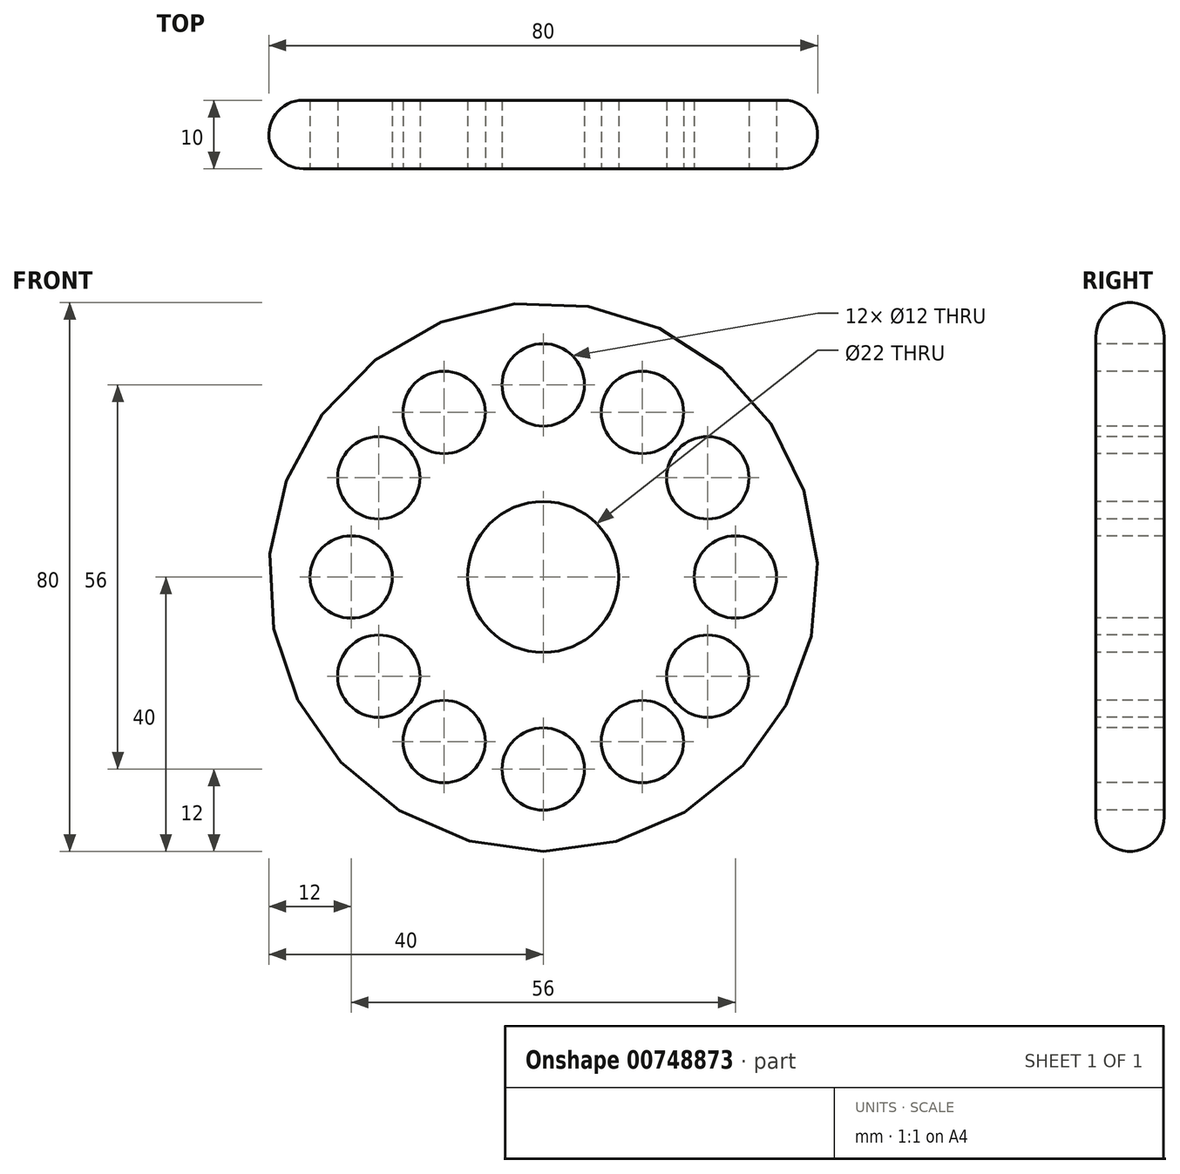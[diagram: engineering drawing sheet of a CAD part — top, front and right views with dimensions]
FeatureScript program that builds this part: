
annotation { "Feature Type Name" : "Feature", "Feature Type Description" : "" }
export const myFeature = defineFeature(function(context is Context, id is Id, definition is map)
    precondition{}
    {
        {
            var Q0;
            Q0=qCreatedBy(makeId("Front.planeOp"),FACE);
            var sketch = newSketch(context, id + "F0", { "sketchPlane" : qUnion([Q0])});
            skCircle(sketch, "E0", {"center": v(0, 0) * mm, "radius": 40 * mm});
            skSolve(sketch);
        }
        {
            var Q0;
            Q0=makeQuery(id+"F0.imprint","IMPRINT",FACE,{"disambiguationData":[TD([[makeQuery(id+"F0.imprint","IMPRINT",EDGE,{"derivedFrom":sQuery(id+"F0.wireOp",EDGE,"E0")}),1.0]])]});
            extrude(context, id + "F1", {"entities" : qUnion([Q0]), "endBound" : BoundingType.SYMMETRIC, "depth" : 10 * mm, "offsetDistance" : 25 * mm});
        }
        {
            var Q0;
            Q0=makeQuery(id+"F1.opExtrude","CAP_FACE",FACE,{"disambiguationData":[OSD([sQuery(id+"F0.wireOp",EDGE,"E0")])],"isStart":false});
            var sketch = newSketch(context, id + "F2", { "sketchPlane" : qUnion([Q0])});
            skPoint(sketch, "E1", {"position": v(0, 0) * mm});
            skPoint(sketch, "E2", {"position": v(-28, 0) * mm});
            skPoint(sketch, "E3", {"position": v(0, -28) * mm});
            skPoint(sketch, "E4", {"position": v(28, 0) * mm});
            skPoint(sketch, "E5", {"position": v(0, 28) * mm});
            skCircle(sketch, "E6", {"center": v(0, 0) * mm, "radius": 28 * mm});
            skPoint(sketch, "E7", {"position": v(-14.45, 23.98) * mm});
            skPoint(sketch, "E8", {"position": v(-23.98, 14.45) * mm});
            skPoint(sketch, "E9", {"position": v(14.45, 23.98) * mm});
            skPoint(sketch, "E10", {"position": v(23.98, 14.45) * mm});
            skPoint(sketch, "E11", {"position": v(23.98, -14.45) * mm});
            skPoint(sketch, "E12", {"position": v(14.45, -23.98) * mm});
            skPoint(sketch, "E13", {"position": v(-14.45, -23.98) * mm});
            skPoint(sketch, "E14", {"position": v(-23.98, -14.45) * mm});
            skSolve(sketch);
        }
        {
            var Q0;
            Q0=sQuery(id+"F2.wireOp",VERTEX,"E1");
            var Q1;
            Q1=makeQuery(id+"F1.opExtrude","SWEPT_BODY",BODY,{"disambiguationData":[OSD([sQuery(id+"F0.wireOp",EDGE,"E0")])]});
            hole(context, id + "F3", {"style" : HoleStyle.SIMPLE, "endStyle" : HoleEndStyle.THROUGH, "holeDiameter" : 22 * mm, "majorDiameter" : 5 * mm, "isTappedThrough" : true, "tappedDepth" : 12 * mm, "tapClearance" : 3, "startFromSketch" : true, "locations" : qUnion([Q0]), "scope" : qUnion([Q1])});
        }
        {
            var Q0;
            Q0=sQuery(id+"F2.wireOp",VERTEX,"E2");
            var Q1;
            Q1=sQuery(id+"F2.wireOp",VERTEX,"E5");
            var Q2;
            Q2=sQuery(id+"F2.wireOp",VERTEX,"E4");
            var Q3;
            Q3=sQuery(id+"F2.wireOp",VERTEX,"E3");
            var Q4;
            Q4=sQuery(id+"F2.wireOp",VERTEX,"52095855-b336-422e-8f80-df5fd629cd5d");
            var Q5;
            Q5=sQuery(id+"F2.wireOp",VERTEX,"24c259f7-befc-4653-8001-a65194ec6784");
            var Q6;
            Q6=sQuery(id+"F2.wireOp",VERTEX,"1d520926-8f3c-40a8-ada0-8b332bf8b6fc");
            var Q7;
            Q7=sQuery(id+"F2.wireOp",VERTEX,"6d6a8224-8775-4271-b540-0e14676ffef5");
            var Q8;
            Q8=sQuery(id+"F2.wireOp",VERTEX,"0255856a-c149-4061-aa0b-9c862e740c1a");
            var Q9;
            Q9=sQuery(id+"F2.wireOp",VERTEX,"93b5c036-bd99-430c-b78d-c26c282c81f6");
            var Q10;
            Q10=sQuery(id+"F2.wireOp",VERTEX,"029029dc-d629-4e09-bd82-9c58e788dda2");
            var Q11;
            Q11=sQuery(id+"F2.wireOp",VERTEX,"19c45f0a-c0c8-45b0-bd96-d868cf0fbe42");
            var Q12;
            Q12=sQuery(id+"F2.wireOp",VERTEX,"E8");
            var Q13;
            Q13=sQuery(id+"F2.wireOp",VERTEX,"E7");
            var Q14;
            Q14=sQuery(id+"F2.wireOp",VERTEX,"E9");
            var Q15;
            Q15=sQuery(id+"F2.wireOp",VERTEX,"E10");
            var Q16;
            Q16=sQuery(id+"F2.wireOp",VERTEX,"E11");
            var Q17;
            Q17=sQuery(id+"F2.wireOp",VERTEX,"E13");
            var Q18;
            Q18=sQuery(id+"F2.wireOp",VERTEX,"E12");
            var Q19;
            Q19=sQuery(id+"F2.wireOp",VERTEX,"E14");
            var Q20;
            Q20=makeQuery(id+"F1.opExtrude","SWEPT_BODY",BODY,{"disambiguationData":[OSD([sQuery(id+"F0.wireOp",EDGE,"E0")])]});
            hole(context, id + "F4", {"style" : HoleStyle.SIMPLE, "endStyle" : HoleEndStyle.THROUGH, "holeDiameter" : 12 * mm, "majorDiameter" : 5 * mm, "isTappedThrough" : true, "tappedDepth" : 12 * mm, "tapClearance" : 3, "startFromSketch" : true, "locations" : qUnion([Q0, Q1, Q2, Q3, Q4, Q5, Q6, Q7, Q8, Q9, Q10, Q11, Q12, Q13, Q14, Q15, Q16, Q17, Q18, Q19]), "scope" : qUnion([Q20])});
        }
        {
            var Q0;
            Q0=makeQuery(id+"F1.opExtrude","CAP_EDGE",EDGE,{"disambiguationData":[OSD([sQuery(id+"F0.wireOp",EDGE,"E0")])],"isStart":false});
            var Q1;
            Q1=makeQuery(id+"F1.opExtrude","SWEPT_FACE",FACE,{"disambiguationData":[OSD([sQuery(id+"F0.wireOp",EDGE,"E0")])]});
            fillet(context, id + "F5", {"entities" : qUnion([Q0, Q1]), "radius" : 5 * mm, "tangentPropagation" : true, "allowEdgeOverflow" : false});
        }
    });
